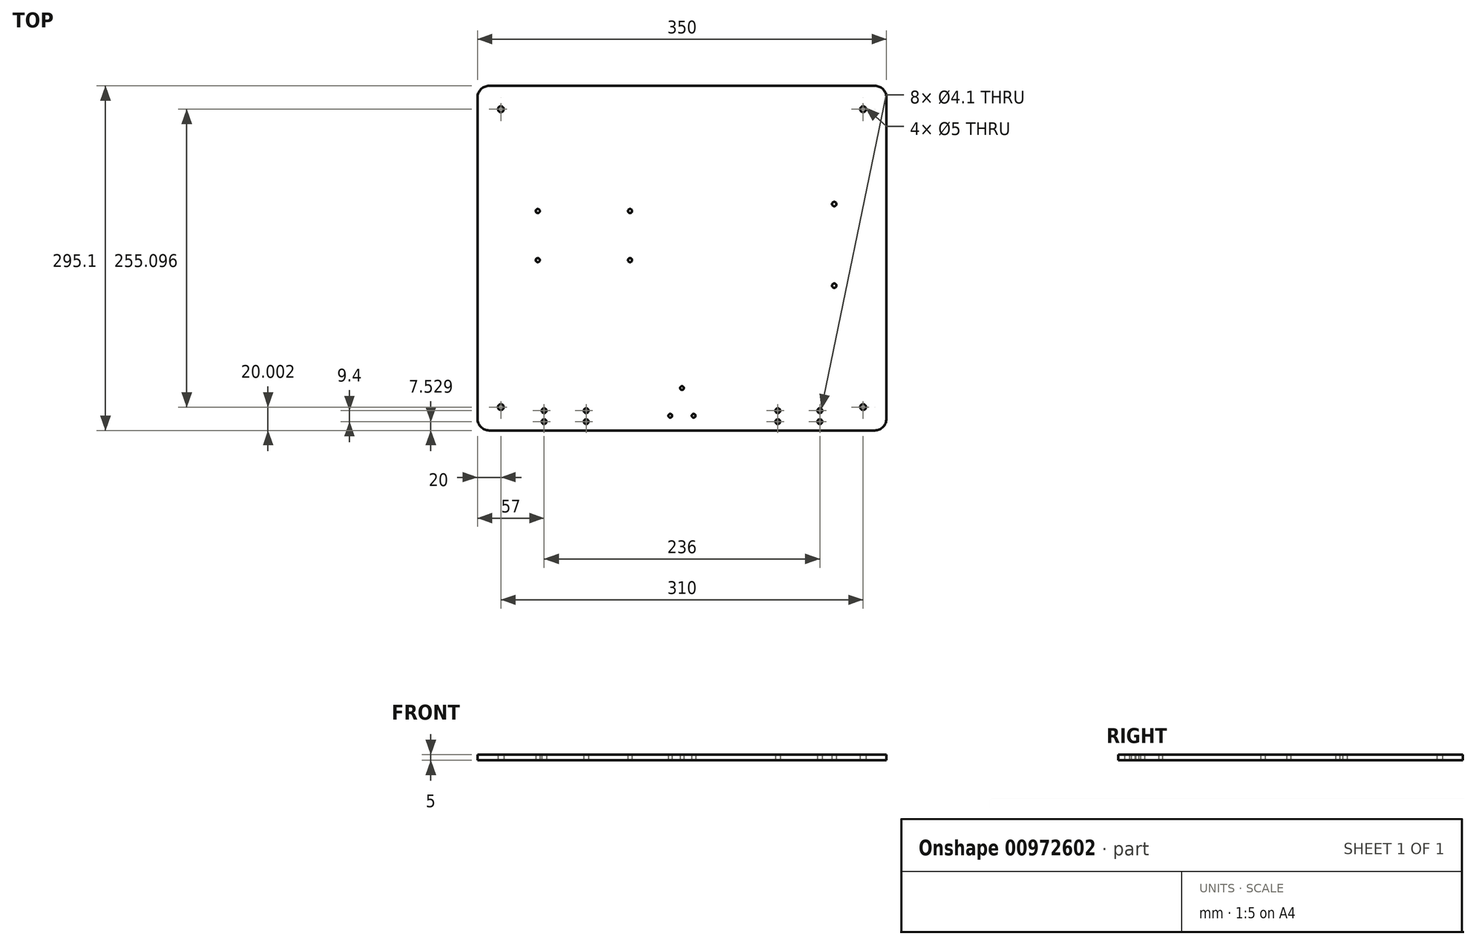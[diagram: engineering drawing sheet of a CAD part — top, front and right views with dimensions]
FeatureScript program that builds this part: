
annotation { "Feature Type Name" : "Feature", "Feature Type Description" : "" }
export const myFeature = defineFeature(function(context is Context, id is Id, definition is map)
    precondition{}
    {
        {
            var Q0;
            Q0=qCreatedBy(makeId("Top.planeOp"),FACE);
            var sketch = newSketch(context, id + "F0", { "sketchPlane" : qUnion([Q0])});
            skLineSegment(sketch, "E0.bottom", {"start": v(-123.44, 58.95) * mm, "end": v(-44.44, 58.95) * mm, "construction": true});
            skLineSegment(sketch, "E0.top", {"start": v(-123.44, 16.95) * mm, "end": v(-44.44, 16.95) * mm, "construction": true});
            skLineSegment(sketch, "E0.left", {"start": v(-123.44, 58.95) * mm, "end": v(-123.44, 16.95) * mm, "construction": true});
            skLineSegment(sketch, "E0.right", {"start": v(-44.44, 58.95) * mm, "end": v(-44.44, 16.95) * mm, "construction": true});
            skCircle(sketch, "E1", {"center": v(-123.44, 58.95) * mm, "radius": 1.75 * mm});
            skCircle(sketch, "E2", {"center": v(-44.44, 58.95) * mm, "radius": 1.75 * mm});
            skCircle(sketch, "E3", {"center": v(-44.44, 16.95) * mm, "radius": 1.75 * mm});
            skCircle(sketch, "E4", {"center": v(-123.44, 16.95) * mm, "radius": 1.75 * mm});
            skLineSegment(sketch, "E5", {"start": v(-83.94, 58.95) * mm, "end": v(-83.94, 16.95) * mm, "construction": true});
            skCircle(sketch, "E6", {"center": v(-10, -116.37) * mm, "radius": 1.6 * mm});
            skCircle(sketch, "E7", {"center": v(10, -116.37) * mm, "radius": 1.6 * mm});
            skCircle(sketch, "E8", {"center": v(0, -92.67) * mm, "radius": 1.6 * mm});
            skLineSegment(sketch, "E9", {"start": v(-10, -116.37) * mm, "end": v(10, -116.37) * mm, "construction": true});
            skPoint(sketch, "E10", {"position": v(0, -116.37) * mm});
            skLineSegment(sketch, "E11", {"start": v(0, -116.37) * mm, "end": v(0, -92.67) * mm, "construction": true});
            skPoint(sketch, "E12", {"position": v(0, -104.52) * mm});
            skCircle(sketch, "E13", {"center": v(-118, -121.4) * mm, "radius": 2.05 * mm});
            skCircle(sketch, "E14", {"center": v(-82, -121.4) * mm, "radius": 2.05 * mm});
            skLineSegment(sketch, "E15", {"start": v(-82, -121.4) * mm, "end": v(-118, -121.4) * mm, "construction": true});
            skLineSegment(sketch, "E16.bottom", {"start": v(-127.5, -125.4) * mm, "end": v(-72.5, -125.4) * mm, "construction": true});
            skLineSegment(sketch, "E16.top", {"start": v(-127.5, -43.7) * mm, "end": v(-72.5, -43.7) * mm, "construction": true});
            skLineSegment(sketch, "E16.left", {"start": v(-127.5, -125.4) * mm, "end": v(-127.5, -43.7) * mm, "construction": true});
            skLineSegment(sketch, "E16.right", {"start": v(-72.5, -125.4) * mm, "end": v(-72.5, -43.7) * mm, "construction": true});
            skLineSegment(sketch, "E17", {"start": v(-100, -125.4) * mm, "end": v(-100, -43.7) * mm, "construction": true});
            skLineSegment(sketch, "E18", {"start": v(-72.5, -84.54) * mm, "end": v(-127.5, -84.54) * mm, "construction": true});
            skPoint(sketch, "E19", {"position": v(-100, -121.4) * mm});
            skCircle(sketch, "E20", {"center": v(-118, -112) * mm, "radius": 2.05 * mm});
            skCircle(sketch, "E21", {"center": v(-82, -112) * mm, "radius": 2.05 * mm});
            skLineSegment(sketch, "E22", {"start": v(-118, -121.4) * mm, "end": v(-118, -112) * mm, "construction": true});
            skLineSegment(sketch, "E23", {"start": v(-82, -112) * mm, "end": v(-82, -121.4) * mm, "construction": true});
            skCircle(sketch, "E24", {"center": v(130.31, 64.96) * mm, "radius": 1.88 * mm});
            skCircle(sketch, "E25", {"center": v(130.31, -5) * mm, "radius": 1.88 * mm});
            skLineSegment(sketch, "E26", {"start": v(130.31, 64.96) * mm, "end": v(130.31, -5) * mm, "construction": true});
            skCircle(sketch, "E27", {"center": v(82, -121.4) * mm, "radius": 2.05 * mm});
            skCircle(sketch, "E28", {"center": v(118, -121.4) * mm, "radius": 2.05 * mm});
            skLineSegment(sketch, "E29", {"start": v(118, -121.4) * mm, "end": v(82, -121.4) * mm, "construction": true});
            skLineSegment(sketch, "E30.bottom", {"start": v(72.5, -125.4) * mm, "end": v(127.5, -125.4) * mm, "construction": true});
            skLineSegment(sketch, "E30.top", {"start": v(72.5, -43.7) * mm, "end": v(127.5, -43.7) * mm, "construction": true});
            skLineSegment(sketch, "E30.left", {"start": v(72.5, -125.4) * mm, "end": v(72.5, -43.7) * mm, "construction": true});
            skLineSegment(sketch, "E30.right", {"start": v(127.5, -125.4) * mm, "end": v(127.5, -43.7) * mm, "construction": true});
            skLineSegment(sketch, "E31", {"start": v(100, -125.4) * mm, "end": v(100, -43.7) * mm, "construction": true});
            skLineSegment(sketch, "E32", {"start": v(127.5, -84.54) * mm, "end": v(72.5, -84.54) * mm, "construction": true});
            skPoint(sketch, "E33", {"position": v(100, -121.4) * mm});
            skCircle(sketch, "E34", {"center": v(82, -112) * mm, "radius": 2.05 * mm});
            skCircle(sketch, "E35", {"center": v(118, -112) * mm, "radius": 2.05 * mm});
            skLineSegment(sketch, "E36", {"start": v(82, -121.4) * mm, "end": v(82, -112) * mm, "construction": true});
            skLineSegment(sketch, "E37", {"start": v(118, -112) * mm, "end": v(118, -121.4) * mm, "construction": true});
            skLineSegment(sketch, "E38.bottom", {"start": v(-113.94, 159.96) * mm, "end": v(26.06, 159.96) * mm, "construction": true});
            skLineSegment(sketch, "E38.top", {"start": v(-113.94, 89.96) * mm, "end": v(26.06, 89.96) * mm, "construction": true});
            skLineSegment(sketch, "E38.left", {"start": v(-113.94, 159.96) * mm, "end": v(-113.94, 89.96) * mm, "construction": true});
            skLineSegment(sketch, "E38.right", {"start": v(26.06, 159.96) * mm, "end": v(26.06, 89.96) * mm, "construction": true});
            skLineSegment(sketch, "E39.bottom", {"start": v(-175, 166.18) * mm, "end": v(175, 166.18) * mm});
            skLineSegment(sketch, "E39.top", {"start": v(-175, -128.92) * mm, "end": v(175, -128.92) * mm});
            skLineSegment(sketch, "E39.left", {"start": v(-175, 166.18) * mm, "end": v(-175, -128.92) * mm});
            skLineSegment(sketch, "E39.right", {"start": v(175, 166.18) * mm, "end": v(175, -128.92) * mm});
            skLineSegment(sketch, "E40", {"start": v(-100, -49.68) * mm, "end": v(100, -49.68) * mm, "construction": true});
            skPoint(sketch, "E41", {"position": v(0, -49.68) * mm});
            skLineSegment(sketch, "E42", {"start": v(0, 0) * mm, "end": v(0, -49.68) * mm, "construction": true});
            skLineSegment(sketch, "E43.bottom", {"start": v(145.31, 74.98) * mm, "end": v(145.31, -15.02) * mm, "construction": true});
            skLineSegment(sketch, "E43.top", {"start": v(50.31, 74.98) * mm, "end": v(50.31, -15.02) * mm, "construction": true});
            skLineSegment(sketch, "E43.left", {"start": v(145.31, 74.98) * mm, "end": v(50.31, 74.98) * mm, "construction": true});
            skLineSegment(sketch, "E43.right", {"start": v(145.31, -15.02) * mm, "end": v(50.31, -15.02) * mm, "construction": true});
            skLineSegment(sketch, "E44", {"start": v(130.31, 29.98) * mm, "end": v(145.31, 29.98) * mm, "construction": true});
            skLineSegment(sketch, "E45", {"start": v(0, 166.18) * mm, "end": v(0, -128.92) * mm, "construction": true});
            skCircle(sketch, "E46", {"center": v(-155, 146.18) * mm, "radius": 2.5 * mm});
            skLineSegment(sketch, "E47", {"start": v(-175, 18.63) * mm, "end": v(175, 18.63) * mm, "construction": true});
            skCircle(sketch, "E48.MirrorC", {"center": v(155, 146.18) * mm, "radius": 2.5 * mm});
            skCircle(sketch, "E49.MirrorC", {"center": v(155, -108.92) * mm, "radius": 2.5 * mm});
            skCircle(sketch, "E50.MirrorC", {"center": v(-155, -108.92) * mm, "radius": 2.5 * mm});
            skSolve(sketch);
        }
        {
            var Q0;
            Q0 = qSketchRegion(id + "F0", true);
            extrude(context, id + "F1", {"entities" : qUnion([Q0]), "depth" : 5 * mm, "offsetDistance" : 25 * mm});
        }
        {
            var Q0;
            Q0=makeQuery(id+"F1.opExtrude","SWEPT_EDGE",EDGE,{"disambiguationData":[OSD([sQuery(id+"F0.wireOp",EDGE,"E39.bottom"),sQuery(id+"F0.wireOp",EDGE,"E39.left")])]});
            var Q1;
            Q1=makeQuery(id+"F1.opExtrude","SWEPT_EDGE",EDGE,{"disambiguationData":[OSD([sQuery(id+"F0.wireOp",EDGE,"E39.top"),sQuery(id+"F0.wireOp",EDGE,"E39.left")])]});
            var Q2;
            Q2=makeQuery(id+"F1.opExtrude","SWEPT_EDGE",EDGE,{"disambiguationData":[OSD([sQuery(id+"F0.wireOp",EDGE,"E39.bottom"),sQuery(id+"F0.wireOp",EDGE,"E39.right")])]});
            var Q3;
            Q3=makeQuery(id+"F1.opExtrude","SWEPT_EDGE",EDGE,{"disambiguationData":[OSD([sQuery(id+"F0.wireOp",EDGE,"E39.top"),sQuery(id+"F0.wireOp",EDGE,"E39.right")])]});
            fillet(context, id + "F2", {"entities" : qUnion([Q0, Q1, Q2, Q3]), "radius" : 10 * mm, "tangentPropagation" : true, "allowEdgeOverflow" : false});
        }
    });
